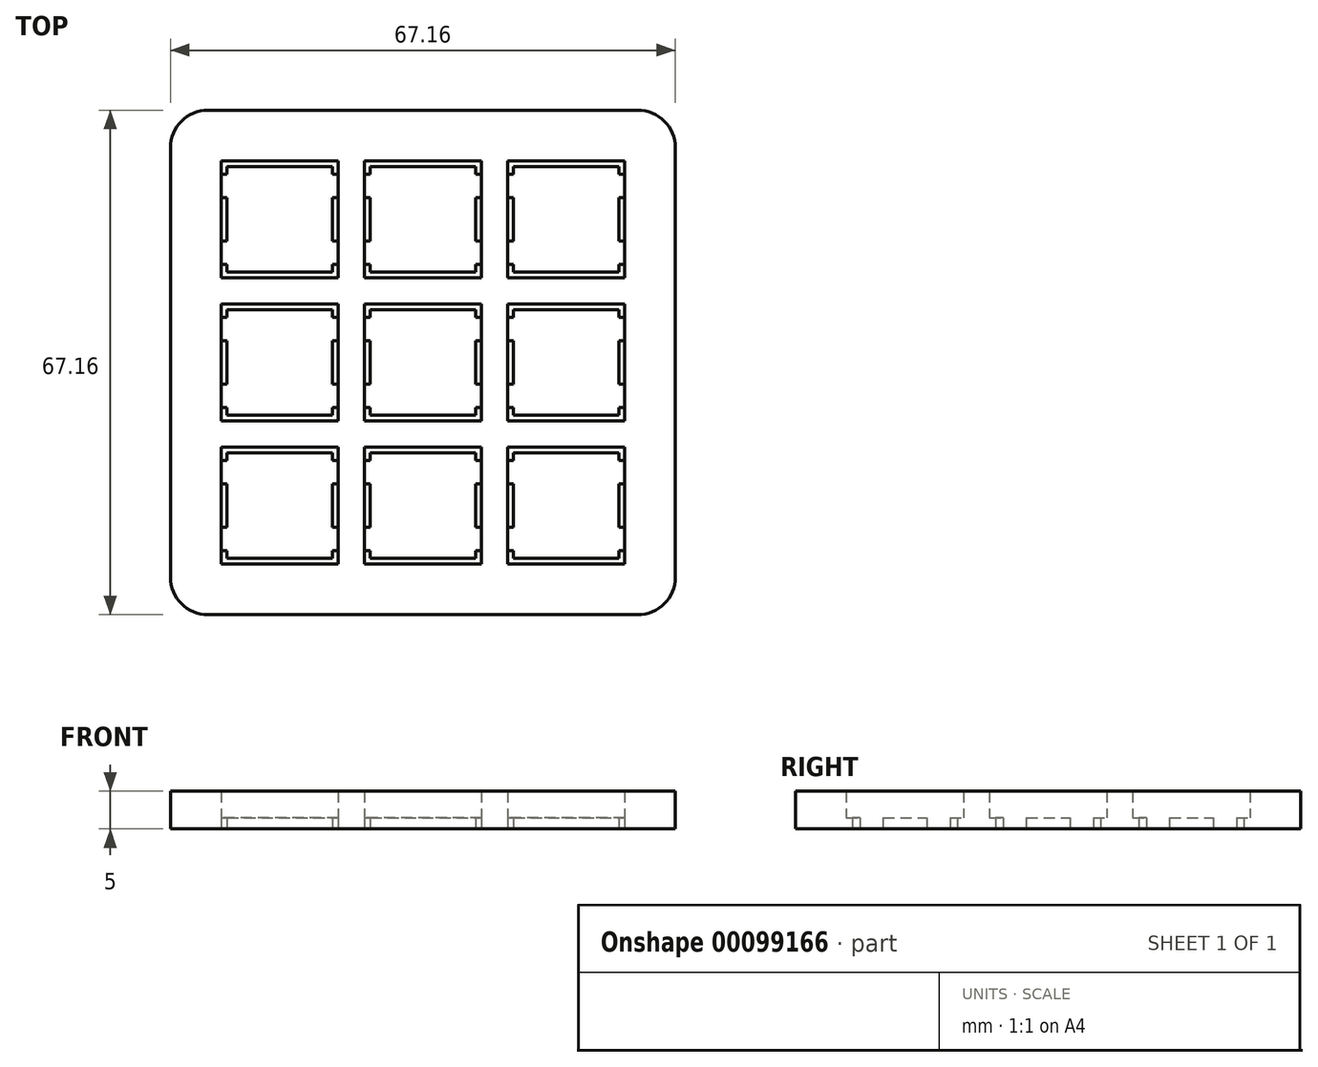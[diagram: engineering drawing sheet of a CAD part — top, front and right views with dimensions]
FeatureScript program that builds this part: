
annotation { "Feature Type Name" : "Feature", "Feature Type Description" : "" }
export const myFeature = defineFeature(function(context is Context, id is Id, definition is map)
    precondition{}
    {
        {
            var Q0;
            Q0=qCreatedBy(makeId("Top.planeOp"),FACE);
            var sketch = newSketch(context, id + "F0", { "sketchPlane" : qUnion([Q0])});
            skLineSegment(sketch, "E0", {"start": v(-33.58, 33.58) * mm, "end": v(33.58, 33.58) * mm});
            skLineSegment(sketch, "E1", {"start": v(33.58, 33.58) * mm, "end": v(33.58, -33.58) * mm});
            skLineSegment(sketch, "E2", {"start": v(33.58, -33.58) * mm, "end": v(-33.58, -33.58) * mm});
            skLineSegment(sketch, "E3", {"start": v(-33.58, -33.58) * mm, "end": v(-33.58, 33.58) * mm});
            skLineSegment(sketch, "E4", {"start": v(-12.05, 13.05) * mm, "end": v(-12.05, 12.05) * mm});
            skLineSegment(sketch, "E5", {"start": v(-12.05, 12.05) * mm, "end": v(-26.05, 12.05) * mm});
            skLineSegment(sketch, "E6", {"start": v(-26.05, 12.05) * mm, "end": v(-26.05, 13.05) * mm});
            skLineSegment(sketch, "E7", {"start": v(-26.05, 13.05) * mm, "end": v(-26.85, 13.05) * mm});
            skLineSegment(sketch, "E8", {"start": v(-26.85, 13.05) * mm, "end": v(-26.85, 16.15) * mm});
            skLineSegment(sketch, "E9", {"start": v(-26.85, 16.15) * mm, "end": v(-26.05, 16.15) * mm});
            skLineSegment(sketch, "E10", {"start": v(-26.05, 16.15) * mm, "end": v(-26.05, 21.95) * mm});
            skLineSegment(sketch, "E11", {"start": v(-26.05, 21.95) * mm, "end": v(-26.85, 21.95) * mm});
            skLineSegment(sketch, "E12", {"start": v(-26.85, 21.95) * mm, "end": v(-26.85, 25.05) * mm});
            skLineSegment(sketch, "E13", {"start": v(-26.85, 25.05) * mm, "end": v(-26.05, 25.05) * mm});
            skLineSegment(sketch, "E14", {"start": v(-26.05, 25.05) * mm, "end": v(-26.05, 26.05) * mm});
            skLineSegment(sketch, "E15", {"start": v(-26.05, 26.05) * mm, "end": v(-12.05, 26.05) * mm});
            skLineSegment(sketch, "E16", {"start": v(-12.05, 26.05) * mm, "end": v(-12.05, 25.05) * mm});
            skLineSegment(sketch, "E17", {"start": v(-12.05, 25.05) * mm, "end": v(-11.25, 25.05) * mm});
            skLineSegment(sketch, "E18", {"start": v(-11.25, 25.05) * mm, "end": v(-11.25, 21.95) * mm});
            skLineSegment(sketch, "E19", {"start": v(-11.25, 21.95) * mm, "end": v(-12.05, 21.95) * mm});
            skLineSegment(sketch, "E20", {"start": v(-12.05, 21.95) * mm, "end": v(-12.05, 16.15) * mm});
            skLineSegment(sketch, "E21", {"start": v(-12.05, 16.15) * mm, "end": v(-11.25, 16.15) * mm});
            skLineSegment(sketch, "E22", {"start": v(-11.25, 16.15) * mm, "end": v(-11.25, 13.05) * mm});
            skLineSegment(sketch, "E23", {"start": v(-11.25, 13.05) * mm, "end": v(-12.05, 13.05) * mm});
            skLineSegment(sketch, "E24", {"start": v(-12.05, -6) * mm, "end": v(-12.05, -7) * mm});
            skLineSegment(sketch, "E25", {"start": v(-12.05, -7) * mm, "end": v(-26.05, -7) * mm});
            skLineSegment(sketch, "E26", {"start": v(-26.05, -7) * mm, "end": v(-26.05, -6) * mm});
            skLineSegment(sketch, "E27", {"start": v(-26.05, -6) * mm, "end": v(-26.85, -6) * mm});
            skLineSegment(sketch, "E28", {"start": v(-26.85, -6) * mm, "end": v(-26.85, -2.9) * mm});
            skLineSegment(sketch, "E29", {"start": v(-26.85, -2.9) * mm, "end": v(-26.05, -2.9) * mm});
            skLineSegment(sketch, "E30", {"start": v(-26.05, -2.9) * mm, "end": v(-26.05, 2.9) * mm});
            skLineSegment(sketch, "E31", {"start": v(-26.05, 2.9) * mm, "end": v(-26.85, 2.9) * mm});
            skLineSegment(sketch, "E32", {"start": v(-26.85, 2.9) * mm, "end": v(-26.85, 6) * mm});
            skLineSegment(sketch, "E33", {"start": v(-26.85, 6) * mm, "end": v(-26.05, 6) * mm});
            skLineSegment(sketch, "E34", {"start": v(-26.05, 6) * mm, "end": v(-26.05, 7) * mm});
            skLineSegment(sketch, "E35", {"start": v(-26.05, 7) * mm, "end": v(-12.05, 7) * mm});
            skLineSegment(sketch, "E36", {"start": v(-12.05, 7) * mm, "end": v(-12.05, 6) * mm});
            skLineSegment(sketch, "E37", {"start": v(-12.05, 6) * mm, "end": v(-11.25, 6) * mm});
            skLineSegment(sketch, "E38", {"start": v(-11.25, 6) * mm, "end": v(-11.25, 2.9) * mm});
            skLineSegment(sketch, "E39", {"start": v(-11.25, 2.9) * mm, "end": v(-12.05, 2.9) * mm});
            skLineSegment(sketch, "E40", {"start": v(-12.05, 2.9) * mm, "end": v(-12.05, -2.9) * mm});
            skLineSegment(sketch, "E41", {"start": v(-12.05, -2.9) * mm, "end": v(-11.25, -2.9) * mm});
            skLineSegment(sketch, "E42", {"start": v(-11.25, -2.9) * mm, "end": v(-11.25, -6) * mm});
            skLineSegment(sketch, "E43", {"start": v(-11.25, -6) * mm, "end": v(-12.05, -6) * mm});
            skLineSegment(sketch, "E44", {"start": v(-12.05, -25.05) * mm, "end": v(-12.05, -26.05) * mm});
            skLineSegment(sketch, "E45", {"start": v(-12.05, -26.05) * mm, "end": v(-26.05, -26.05) * mm});
            skLineSegment(sketch, "E46", {"start": v(-26.05, -26.05) * mm, "end": v(-26.05, -25.05) * mm});
            skLineSegment(sketch, "E47", {"start": v(-26.05, -25.05) * mm, "end": v(-26.85, -25.05) * mm});
            skLineSegment(sketch, "E48", {"start": v(-26.85, -25.05) * mm, "end": v(-26.85, -21.95) * mm});
            skLineSegment(sketch, "E49", {"start": v(-26.85, -21.95) * mm, "end": v(-26.05, -21.95) * mm});
            skLineSegment(sketch, "E50", {"start": v(-26.05, -21.95) * mm, "end": v(-26.05, -16.15) * mm});
            skLineSegment(sketch, "E51", {"start": v(-26.05, -16.15) * mm, "end": v(-26.85, -16.15) * mm});
            skLineSegment(sketch, "E52", {"start": v(-26.85, -16.15) * mm, "end": v(-26.85, -13.05) * mm});
            skLineSegment(sketch, "E53", {"start": v(-26.85, -13.05) * mm, "end": v(-26.05, -13.05) * mm});
            skLineSegment(sketch, "E54", {"start": v(-26.05, -13.05) * mm, "end": v(-26.05, -12.05) * mm});
            skLineSegment(sketch, "E55", {"start": v(-26.05, -12.05) * mm, "end": v(-12.05, -12.05) * mm});
            skLineSegment(sketch, "E56", {"start": v(-12.05, -12.05) * mm, "end": v(-12.05, -13.05) * mm});
            skLineSegment(sketch, "E57", {"start": v(-12.05, -13.05) * mm, "end": v(-11.25, -13.05) * mm});
            skLineSegment(sketch, "E58", {"start": v(-11.25, -13.05) * mm, "end": v(-11.25, -16.15) * mm});
            skLineSegment(sketch, "E59", {"start": v(-11.25, -16.15) * mm, "end": v(-12.05, -16.15) * mm});
            skLineSegment(sketch, "E60", {"start": v(-12.05, -16.15) * mm, "end": v(-12.05, -21.95) * mm});
            skLineSegment(sketch, "E61", {"start": v(-12.05, -21.95) * mm, "end": v(-11.25, -21.95) * mm});
            skLineSegment(sketch, "E62", {"start": v(-11.25, -21.95) * mm, "end": v(-11.25, -25.05) * mm});
            skLineSegment(sketch, "E63", {"start": v(-11.25, -25.05) * mm, "end": v(-12.05, -25.05) * mm});
            skLineSegment(sketch, "E64", {"start": v(7, 13.05) * mm, "end": v(7, 12.05) * mm});
            skLineSegment(sketch, "E65", {"start": v(7, 12.05) * mm, "end": v(-7, 12.05) * mm});
            skLineSegment(sketch, "E66", {"start": v(-7, 12.05) * mm, "end": v(-7, 13.05) * mm});
            skLineSegment(sketch, "E67", {"start": v(-7, 13.05) * mm, "end": v(-7.8, 13.05) * mm});
            skLineSegment(sketch, "E68", {"start": v(-7.8, 13.05) * mm, "end": v(-7.8, 16.15) * mm});
            skLineSegment(sketch, "E69", {"start": v(-7.8, 16.15) * mm, "end": v(-7, 16.15) * mm});
            skLineSegment(sketch, "E70", {"start": v(-7, 16.15) * mm, "end": v(-7, 21.95) * mm});
            skLineSegment(sketch, "E71", {"start": v(-7, 21.95) * mm, "end": v(-7.8, 21.95) * mm});
            skLineSegment(sketch, "E72", {"start": v(-7.8, 21.95) * mm, "end": v(-7.8, 25.05) * mm});
            skLineSegment(sketch, "E73", {"start": v(-7.8, 25.05) * mm, "end": v(-7, 25.05) * mm});
            skLineSegment(sketch, "E74", {"start": v(-7, 25.05) * mm, "end": v(-7, 26.05) * mm});
            skLineSegment(sketch, "E75", {"start": v(-7, 26.05) * mm, "end": v(7, 26.05) * mm});
            skLineSegment(sketch, "E76", {"start": v(7, 26.05) * mm, "end": v(7, 25.05) * mm});
            skLineSegment(sketch, "E77", {"start": v(7, 25.05) * mm, "end": v(7.8, 25.05) * mm});
            skLineSegment(sketch, "E78", {"start": v(7.8, 25.05) * mm, "end": v(7.8, 21.95) * mm});
            skLineSegment(sketch, "E79", {"start": v(7.8, 21.95) * mm, "end": v(7, 21.95) * mm});
            skLineSegment(sketch, "E80", {"start": v(7, 21.95) * mm, "end": v(7, 16.15) * mm});
            skLineSegment(sketch, "E81", {"start": v(7, 16.15) * mm, "end": v(7.8, 16.15) * mm});
            skLineSegment(sketch, "E82", {"start": v(7.8, 16.15) * mm, "end": v(7.8, 13.05) * mm});
            skLineSegment(sketch, "E83", {"start": v(7.8, 13.05) * mm, "end": v(7, 13.05) * mm});
            skLineSegment(sketch, "E84", {"start": v(7, -6) * mm, "end": v(7, -7) * mm});
            skLineSegment(sketch, "E85", {"start": v(7, -7) * mm, "end": v(-7, -7) * mm});
            skLineSegment(sketch, "E86", {"start": v(-7, -7) * mm, "end": v(-7, -6) * mm});
            skLineSegment(sketch, "E87", {"start": v(-7, -6) * mm, "end": v(-7.8, -6) * mm});
            skLineSegment(sketch, "E88", {"start": v(-7.8, -6) * mm, "end": v(-7.8, -2.9) * mm});
            skLineSegment(sketch, "E89", {"start": v(-7.8, -2.9) * mm, "end": v(-7, -2.9) * mm});
            skLineSegment(sketch, "E90", {"start": v(-7, -2.9) * mm, "end": v(-7, 2.9) * mm});
            skLineSegment(sketch, "E91", {"start": v(-7, 2.9) * mm, "end": v(-7.8, 2.9) * mm});
            skLineSegment(sketch, "E92", {"start": v(-7.8, 2.9) * mm, "end": v(-7.8, 6) * mm});
            skLineSegment(sketch, "E93", {"start": v(-7.8, 6) * mm, "end": v(-7, 6) * mm});
            skLineSegment(sketch, "E94", {"start": v(-7, 6) * mm, "end": v(-7, 7) * mm});
            skLineSegment(sketch, "E95", {"start": v(-7, 7) * mm, "end": v(7, 7) * mm});
            skLineSegment(sketch, "E96", {"start": v(7, 7) * mm, "end": v(7, 6) * mm});
            skLineSegment(sketch, "E97", {"start": v(7, 6) * mm, "end": v(7.8, 6) * mm});
            skLineSegment(sketch, "E98", {"start": v(7.8, 6) * mm, "end": v(7.8, 2.9) * mm});
            skLineSegment(sketch, "E99", {"start": v(7.8, 2.9) * mm, "end": v(7, 2.9) * mm});
            skLineSegment(sketch, "E100", {"start": v(7, 2.9) * mm, "end": v(7, -2.9) * mm});
            skLineSegment(sketch, "E101", {"start": v(7, -2.9) * mm, "end": v(7.8, -2.9) * mm});
            skLineSegment(sketch, "E102", {"start": v(7.8, -2.9) * mm, "end": v(7.8, -6) * mm});
            skLineSegment(sketch, "E103", {"start": v(7.8, -6) * mm, "end": v(7, -6) * mm});
            skLineSegment(sketch, "E104", {"start": v(7, -25.05) * mm, "end": v(7, -26.05) * mm});
            skLineSegment(sketch, "E105", {"start": v(7, -26.05) * mm, "end": v(-7, -26.05) * mm});
            skLineSegment(sketch, "E106", {"start": v(-7, -26.05) * mm, "end": v(-7, -25.05) * mm});
            skLineSegment(sketch, "E107", {"start": v(-7, -25.05) * mm, "end": v(-7.8, -25.05) * mm});
            skLineSegment(sketch, "E108", {"start": v(-7.8, -25.05) * mm, "end": v(-7.8, -21.95) * mm});
            skLineSegment(sketch, "E109", {"start": v(-7.8, -21.95) * mm, "end": v(-7, -21.95) * mm});
            skLineSegment(sketch, "E110", {"start": v(-7, -21.95) * mm, "end": v(-7, -16.15) * mm});
            skLineSegment(sketch, "E111", {"start": v(-7, -16.15) * mm, "end": v(-7.8, -16.15) * mm});
            skLineSegment(sketch, "E112", {"start": v(-7.8, -16.15) * mm, "end": v(-7.8, -13.05) * mm});
            skLineSegment(sketch, "E113", {"start": v(-7.8, -13.05) * mm, "end": v(-7, -13.05) * mm});
            skLineSegment(sketch, "E114", {"start": v(-7, -13.05) * mm, "end": v(-7, -12.05) * mm});
            skLineSegment(sketch, "E115", {"start": v(-7, -12.05) * mm, "end": v(7, -12.05) * mm});
            skLineSegment(sketch, "E116", {"start": v(7, -12.05) * mm, "end": v(7, -13.05) * mm});
            skLineSegment(sketch, "E117", {"start": v(7, -13.05) * mm, "end": v(7.8, -13.05) * mm});
            skLineSegment(sketch, "E118", {"start": v(7.8, -13.05) * mm, "end": v(7.8, -16.15) * mm});
            skLineSegment(sketch, "E119", {"start": v(7.8, -16.15) * mm, "end": v(7, -16.15) * mm});
            skLineSegment(sketch, "E120", {"start": v(7, -16.15) * mm, "end": v(7, -21.95) * mm});
            skLineSegment(sketch, "E121", {"start": v(7, -21.95) * mm, "end": v(7.8, -21.95) * mm});
            skLineSegment(sketch, "E122", {"start": v(7.8, -21.95) * mm, "end": v(7.8, -25.05) * mm});
            skLineSegment(sketch, "E123", {"start": v(7.8, -25.05) * mm, "end": v(7, -25.05) * mm});
            skLineSegment(sketch, "E124", {"start": v(26.05, 13.05) * mm, "end": v(26.05, 12.05) * mm});
            skLineSegment(sketch, "E125", {"start": v(26.05, 12.05) * mm, "end": v(12.05, 12.05) * mm});
            skLineSegment(sketch, "E126", {"start": v(12.05, 12.05) * mm, "end": v(12.05, 13.05) * mm});
            skLineSegment(sketch, "E127", {"start": v(12.05, 13.05) * mm, "end": v(11.25, 13.05) * mm});
            skLineSegment(sketch, "E128", {"start": v(11.25, 13.05) * mm, "end": v(11.25, 16.15) * mm});
            skLineSegment(sketch, "E129", {"start": v(11.25, 16.15) * mm, "end": v(12.05, 16.15) * mm});
            skLineSegment(sketch, "E130", {"start": v(12.05, 16.15) * mm, "end": v(12.05, 21.95) * mm});
            skLineSegment(sketch, "E131", {"start": v(12.05, 21.95) * mm, "end": v(11.25, 21.95) * mm});
            skLineSegment(sketch, "E132", {"start": v(11.25, 21.95) * mm, "end": v(11.25, 25.05) * mm});
            skLineSegment(sketch, "E133", {"start": v(11.25, 25.05) * mm, "end": v(12.05, 25.05) * mm});
            skLineSegment(sketch, "E134", {"start": v(12.05, 25.05) * mm, "end": v(12.05, 26.05) * mm});
            skLineSegment(sketch, "E135", {"start": v(12.05, 26.05) * mm, "end": v(26.05, 26.05) * mm});
            skLineSegment(sketch, "E136", {"start": v(26.05, 26.05) * mm, "end": v(26.05, 25.05) * mm});
            skLineSegment(sketch, "E137", {"start": v(26.05, 25.05) * mm, "end": v(26.85, 25.05) * mm});
            skLineSegment(sketch, "E138", {"start": v(26.85, 25.05) * mm, "end": v(26.85, 21.95) * mm});
            skLineSegment(sketch, "E139", {"start": v(26.85, 21.95) * mm, "end": v(26.05, 21.95) * mm});
            skLineSegment(sketch, "E140", {"start": v(26.05, 21.95) * mm, "end": v(26.05, 16.15) * mm});
            skLineSegment(sketch, "E141", {"start": v(26.05, 16.15) * mm, "end": v(26.85, 16.15) * mm});
            skLineSegment(sketch, "E142", {"start": v(26.85, 16.15) * mm, "end": v(26.85, 13.05) * mm});
            skLineSegment(sketch, "E143", {"start": v(26.85, 13.05) * mm, "end": v(26.05, 13.05) * mm});
            skLineSegment(sketch, "E144", {"start": v(26.05, -6) * mm, "end": v(26.05, -7) * mm});
            skLineSegment(sketch, "E145", {"start": v(26.05, -7) * mm, "end": v(12.05, -7) * mm});
            skLineSegment(sketch, "E146", {"start": v(12.05, -7) * mm, "end": v(12.05, -6) * mm});
            skLineSegment(sketch, "E147", {"start": v(12.05, -6) * mm, "end": v(11.25, -6) * mm});
            skLineSegment(sketch, "E148", {"start": v(11.25, -6) * mm, "end": v(11.25, -2.9) * mm});
            skLineSegment(sketch, "E149", {"start": v(11.25, -2.9) * mm, "end": v(12.05, -2.9) * mm});
            skLineSegment(sketch, "E150", {"start": v(12.05, -2.9) * mm, "end": v(12.05, 2.9) * mm});
            skLineSegment(sketch, "E151", {"start": v(12.05, 2.9) * mm, "end": v(11.25, 2.9) * mm});
            skLineSegment(sketch, "E152", {"start": v(11.25, 2.9) * mm, "end": v(11.25, 6) * mm});
            skLineSegment(sketch, "E153", {"start": v(11.25, 6) * mm, "end": v(12.05, 6) * mm});
            skLineSegment(sketch, "E154", {"start": v(12.05, 6) * mm, "end": v(12.05, 7) * mm});
            skLineSegment(sketch, "E155", {"start": v(12.05, 7) * mm, "end": v(26.05, 7) * mm});
            skLineSegment(sketch, "E156", {"start": v(26.05, 7) * mm, "end": v(26.05, 6) * mm});
            skLineSegment(sketch, "E157", {"start": v(26.05, 6) * mm, "end": v(26.85, 6) * mm});
            skLineSegment(sketch, "E158", {"start": v(26.85, 6) * mm, "end": v(26.85, 2.9) * mm});
            skLineSegment(sketch, "E159", {"start": v(26.85, 2.9) * mm, "end": v(26.05, 2.9) * mm});
            skLineSegment(sketch, "E160", {"start": v(26.05, 2.9) * mm, "end": v(26.05, -2.9) * mm});
            skLineSegment(sketch, "E161", {"start": v(26.05, -2.9) * mm, "end": v(26.85, -2.9) * mm});
            skLineSegment(sketch, "E162", {"start": v(26.85, -2.9) * mm, "end": v(26.85, -6) * mm});
            skLineSegment(sketch, "E163", {"start": v(26.85, -6) * mm, "end": v(26.05, -6) * mm});
            skLineSegment(sketch, "E164", {"start": v(26.05, -25.05) * mm, "end": v(26.05, -26.05) * mm});
            skLineSegment(sketch, "E165", {"start": v(26.05, -26.05) * mm, "end": v(12.05, -26.05) * mm});
            skLineSegment(sketch, "E166", {"start": v(12.05, -26.05) * mm, "end": v(12.05, -25.05) * mm});
            skLineSegment(sketch, "E167", {"start": v(12.05, -25.05) * mm, "end": v(11.25, -25.05) * mm});
            skLineSegment(sketch, "E168", {"start": v(11.25, -25.05) * mm, "end": v(11.25, -21.95) * mm});
            skLineSegment(sketch, "E169", {"start": v(11.25, -21.95) * mm, "end": v(12.05, -21.95) * mm});
            skLineSegment(sketch, "E170", {"start": v(12.05, -21.95) * mm, "end": v(12.05, -16.15) * mm});
            skLineSegment(sketch, "E171", {"start": v(12.05, -16.15) * mm, "end": v(11.25, -16.15) * mm});
            skLineSegment(sketch, "E172", {"start": v(11.25, -16.15) * mm, "end": v(11.25, -13.05) * mm});
            skLineSegment(sketch, "E173", {"start": v(11.25, -13.05) * mm, "end": v(12.05, -13.05) * mm});
            skLineSegment(sketch, "E174", {"start": v(12.05, -13.05) * mm, "end": v(12.05, -12.05) * mm});
            skLineSegment(sketch, "E175", {"start": v(12.05, -12.05) * mm, "end": v(26.05, -12.05) * mm});
            skLineSegment(sketch, "E176", {"start": v(26.05, -12.05) * mm, "end": v(26.05, -13.05) * mm});
            skLineSegment(sketch, "E177", {"start": v(26.05, -13.05) * mm, "end": v(26.85, -13.05) * mm});
            skLineSegment(sketch, "E178", {"start": v(26.85, -13.05) * mm, "end": v(26.85, -16.15) * mm});
            skLineSegment(sketch, "E179", {"start": v(26.85, -16.15) * mm, "end": v(26.05, -16.15) * mm});
            skLineSegment(sketch, "E180", {"start": v(26.05, -16.15) * mm, "end": v(26.05, -21.95) * mm});
            skLineSegment(sketch, "E181", {"start": v(26.05, -21.95) * mm, "end": v(26.85, -21.95) * mm});
            skLineSegment(sketch, "E182", {"start": v(26.85, -21.95) * mm, "end": v(26.85, -25.05) * mm});
            skLineSegment(sketch, "E183", {"start": v(26.85, -25.05) * mm, "end": v(26.05, -25.05) * mm});
            skLineSegment(sketch, "E184", {"start": v(-40.38, 26.85) * mm, "end": v(39.04, 26.85) * mm, "construction": true});
            skLineSegment(sketch, "E185.MirrorCS", {"start": v(-40.38, -26.85) * mm, "end": v(39.04, -26.85) * mm, "construction": true});
            skLineSegment(sketch, "E186", {"start": v(39.04, 11.25) * mm, "end": v(-40.38, 11.25) * mm, "construction": true});
            skLineSegment(sketch, "E187.MirrorCS", {"start": v(39.04, -11.25) * mm, "end": v(-40.38, -11.25) * mm, "construction": true});
            skLineSegment(sketch, "E188", {"start": v(39.04, 11.25) * mm, "end": v(39.04, 7.8) * mm, "construction": true});
            skLineSegment(sketch, "E189", {"start": v(39.04, 7.8) * mm, "end": v(-40.38, 7.8) * mm, "construction": true});
            skLineSegment(sketch, "E190.MirrorCS", {"start": v(39.04, -7.8) * mm, "end": v(-40.38, -7.8) * mm, "construction": true});
            skLineSegment(sketch, "E191.bottom", {"start": v(-26.85, 26.85) * mm, "end": v(-11.25, 26.85) * mm});
            skLineSegment(sketch, "E191.top", {"start": v(-26.85, 11.25) * mm, "end": v(-11.25, 11.25) * mm});
            skLineSegment(sketch, "E191.left", {"start": v(-26.85, 26.85) * mm, "end": v(-26.85, 11.25) * mm});
            skLineSegment(sketch, "E191.right", {"start": v(-11.25, 26.85) * mm, "end": v(-11.25, 11.25) * mm});
            skLineSegment(sketch, "E192.bottom", {"start": v(-7.8, 26.85) * mm, "end": v(7.8, 26.85) * mm});
            skLineSegment(sketch, "E192.top", {"start": v(-7.8, 11.25) * mm, "end": v(7.8, 11.25) * mm});
            skLineSegment(sketch, "E192.left", {"start": v(-7.8, 26.85) * mm, "end": v(-7.8, 11.25) * mm});
            skLineSegment(sketch, "E192.right", {"start": v(7.8, 26.85) * mm, "end": v(7.8, 11.25) * mm});
            skLineSegment(sketch, "E193.bottom", {"start": v(11.25, 26.85) * mm, "end": v(26.85, 26.85) * mm});
            skLineSegment(sketch, "E193.top", {"start": v(11.25, 11.25) * mm, "end": v(26.85, 11.25) * mm});
            skLineSegment(sketch, "E193.left", {"start": v(11.25, 26.85) * mm, "end": v(11.25, 11.25) * mm});
            skLineSegment(sketch, "E193.right", {"start": v(26.85, 26.85) * mm, "end": v(26.85, 11.25) * mm});
            skLineSegment(sketch, "E194.bottom", {"start": v(-26.85, 7.8) * mm, "end": v(-11.25, 7.8) * mm});
            skLineSegment(sketch, "E194.top", {"start": v(-26.85, -7.8) * mm, "end": v(-11.25, -7.8) * mm});
            skLineSegment(sketch, "E194.left", {"start": v(-26.85, 7.8) * mm, "end": v(-26.85, -7.8) * mm});
            skLineSegment(sketch, "E194.right", {"start": v(-11.25, 7.8) * mm, "end": v(-11.25, -7.8) * mm});
            skLineSegment(sketch, "E195.bottom", {"start": v(-7.8, 7.8) * mm, "end": v(7.8, 7.8) * mm});
            skLineSegment(sketch, "E195.top", {"start": v(-7.8, -7.8) * mm, "end": v(7.8, -7.8) * mm});
            skLineSegment(sketch, "E195.left", {"start": v(-7.8, 7.8) * mm, "end": v(-7.8, -7.8) * mm});
            skLineSegment(sketch, "E195.right", {"start": v(7.8, 7.8) * mm, "end": v(7.8, -7.8) * mm});
            skLineSegment(sketch, "E196.bottom", {"start": v(11.25, 7.8) * mm, "end": v(26.85, 7.8) * mm});
            skLineSegment(sketch, "E196.top", {"start": v(11.25, -7.8) * mm, "end": v(26.85, -7.8) * mm});
            skLineSegment(sketch, "E196.left", {"start": v(11.25, 7.8) * mm, "end": v(11.25, -7.8) * mm});
            skLineSegment(sketch, "E196.right", {"start": v(26.85, 7.8) * mm, "end": v(26.85, -7.8) * mm});
            skLineSegment(sketch, "E197.bottom", {"start": v(-26.85, -11.25) * mm, "end": v(-11.25, -11.25) * mm});
            skLineSegment(sketch, "E197.top", {"start": v(-26.85, -26.85) * mm, "end": v(-11.25, -26.85) * mm});
            skLineSegment(sketch, "E197.left", {"start": v(-26.85, -11.25) * mm, "end": v(-26.85, -26.85) * mm});
            skLineSegment(sketch, "E197.right", {"start": v(-11.25, -11.25) * mm, "end": v(-11.25, -26.85) * mm});
            skLineSegment(sketch, "E198.bottom", {"start": v(-7.8, -11.25) * mm, "end": v(7.8, -11.25) * mm});
            skLineSegment(sketch, "E198.top", {"start": v(-7.8, -26.85) * mm, "end": v(7.8, -26.85) * mm});
            skLineSegment(sketch, "E198.left", {"start": v(-7.8, -11.25) * mm, "end": v(-7.8, -26.85) * mm});
            skLineSegment(sketch, "E198.right", {"start": v(7.8, -11.25) * mm, "end": v(7.8, -26.85) * mm});
            skLineSegment(sketch, "E199.bottom", {"start": v(11.25, -11.25) * mm, "end": v(26.85, -11.25) * mm});
            skLineSegment(sketch, "E199.top", {"start": v(11.25, -26.85) * mm, "end": v(26.85, -26.85) * mm});
            skLineSegment(sketch, "E199.left", {"start": v(11.25, -11.25) * mm, "end": v(11.25, -26.85) * mm});
            skLineSegment(sketch, "E199.right", {"start": v(26.85, -11.25) * mm, "end": v(26.85, -26.85) * mm});
            skSolve(sketch);
        }
        {
            var Q0;
            Q0=makeQuery(id+"F0.imprint","IMPRINT",FACE,{"disambiguationData":[TD([[makeQuery(id+"F0.imprint","IMPRINT",EDGE,{"derivedFrom":sQuery(id+"F0.wireOp",EDGE,"E0")}),-1.0]])]});
            var Q1;
            {var subQ0=sQuery(id+"F0.wireOp",EDGE,"E9");Q1=makeQuery(id+"F0.imprint","IMPRINT",FACE,{"disambiguationData":[TD([[makeQuery(id+"F0.imprint","IMPRINT",EDGE,{"derivedFrom":subQ0}),1.0]])]});}
            var Q2;
            {var subQ4=sQuery(id+"F0.wireOp",EDGE,"E13");Q2=makeQuery(id+"F0.imprint","IMPRINT",FACE,{"disambiguationData":[TD([[makeQuery(id+"F0.imprint","IMPRINT",EDGE,{"derivedFrom":subQ4}),1.0]])]});}
            var Q3;
            {var subQ0=sQuery(id+"F0.wireOp",EDGE,"E19");Q3=makeQuery(id+"F0.imprint","IMPRINT",FACE,{"disambiguationData":[TD([[makeQuery(id+"F0.imprint","IMPRINT",EDGE,{"derivedFrom":subQ0}),1.0]])]});}
            var Q4;
            Q4=makeQuery(id+"F0.imprint","IMPRINT",FACE,{"disambiguationData":[TD([[makeQuery(id+"F0.imprint","IMPRINT",EDGE,{"derivedFrom":sQuery(id+"F0.wireOp",EDGE,"E4")}),1.0]])]});
            var Q5;
            Q5=makeQuery(id+"F0.imprint","IMPRINT",FACE,{"disambiguationData":[TD([[makeQuery(id+"F0.imprint","IMPRINT",EDGE,{"derivedFrom":sQuery(id+"F0.wireOp",EDGE,"E64")}),1.0]])]});
            var Q6;
            {var subQ0=sQuery(id+"F0.wireOp",EDGE,"E69");Q6=makeQuery(id+"F0.imprint","IMPRINT",FACE,{"disambiguationData":[TD([[makeQuery(id+"F0.imprint","IMPRINT",EDGE,{"derivedFrom":subQ0}),1.0]])]});}
            var Q7;
            {var subQ0=sQuery(id+"F0.wireOp",EDGE,"E73");Q7=makeQuery(id+"F0.imprint","IMPRINT",FACE,{"disambiguationData":[TD([[makeQuery(id+"F0.imprint","IMPRINT",EDGE,{"derivedFrom":subQ0}),1.0]])]});}
            var Q8;
            {var subQ0=sQuery(id+"F0.wireOp",EDGE,"E79");Q8=makeQuery(id+"F0.imprint","IMPRINT",FACE,{"disambiguationData":[TD([[makeQuery(id+"F0.imprint","IMPRINT",EDGE,{"derivedFrom":subQ0}),1.0]])]});}
            var Q9;
            {var subQ0=sQuery(id+"F0.wireOp",EDGE,"E129");Q9=makeQuery(id+"F0.imprint","IMPRINT",FACE,{"disambiguationData":[TD([[makeQuery(id+"F0.imprint","IMPRINT",EDGE,{"derivedFrom":subQ0}),1.0]])]});}
            var Q10;
            {var subQ3=sQuery(id+"F0.wireOp",EDGE,"E133");Q10=makeQuery(id+"F0.imprint","IMPRINT",FACE,{"disambiguationData":[TD([[makeQuery(id+"F0.imprint","IMPRINT",EDGE,{"derivedFrom":subQ3}),1.0]])]});}
            var Q11;
            {var subQ0=sQuery(id+"F0.wireOp",EDGE,"E139");Q11=makeQuery(id+"F0.imprint","IMPRINT",FACE,{"disambiguationData":[TD([[makeQuery(id+"F0.imprint","IMPRINT",EDGE,{"derivedFrom":subQ0}),1.0]])]});}
            var Q12;
            Q12=makeQuery(id+"F0.imprint","IMPRINT",FACE,{"disambiguationData":[TD([[makeQuery(id+"F0.imprint","IMPRINT",EDGE,{"derivedFrom":sQuery(id+"F0.wireOp",EDGE,"E124")}),1.0]])]});
            var Q13;
            {var subQ0=sQuery(id+"F0.wireOp",EDGE,"E153");Q13=makeQuery(id+"F0.imprint","IMPRINT",FACE,{"disambiguationData":[TD([[makeQuery(id+"F0.imprint","IMPRINT",EDGE,{"derivedFrom":subQ0}),1.0]])]});}
            var Q14;
            {var subQ0=sQuery(id+"F0.wireOp",EDGE,"E149");Q14=makeQuery(id+"F0.imprint","IMPRINT",FACE,{"disambiguationData":[TD([[makeQuery(id+"F0.imprint","IMPRINT",EDGE,{"derivedFrom":subQ0}),1.0]])]});}
            var Q15;
            {var subQ0=sQuery(id+"F0.wireOp",EDGE,"E159");Q15=makeQuery(id+"F0.imprint","IMPRINT",FACE,{"disambiguationData":[TD([[makeQuery(id+"F0.imprint","IMPRINT",EDGE,{"derivedFrom":subQ0}),1.0]])]});}
            var Q16;
            Q16=makeQuery(id+"F0.imprint","IMPRINT",FACE,{"disambiguationData":[TD([[makeQuery(id+"F0.imprint","IMPRINT",EDGE,{"derivedFrom":sQuery(id+"F0.wireOp",EDGE,"E144")}),1.0]])]});
            var Q17;
            Q17=makeQuery(id+"F0.imprint","IMPRINT",FACE,{"disambiguationData":[TD([[makeQuery(id+"F0.imprint","IMPRINT",EDGE,{"derivedFrom":sQuery(id+"F0.wireOp",EDGE,"E84")}),1.0]])]});
            var Q18;
            {var subQ0=sQuery(id+"F0.wireOp",EDGE,"E99");Q18=makeQuery(id+"F0.imprint","IMPRINT",FACE,{"disambiguationData":[TD([[makeQuery(id+"F0.imprint","IMPRINT",EDGE,{"derivedFrom":subQ0}),1.0]])]});}
            var Q19;
            {var subQ0=sQuery(id+"F0.wireOp",EDGE,"E93");Q19=makeQuery(id+"F0.imprint","IMPRINT",FACE,{"disambiguationData":[TD([[makeQuery(id+"F0.imprint","IMPRINT",EDGE,{"derivedFrom":subQ0}),1.0]])]});}
            var Q20;
            {var subQ0=sQuery(id+"F0.wireOp",EDGE,"E89");Q20=makeQuery(id+"F0.imprint","IMPRINT",FACE,{"disambiguationData":[TD([[makeQuery(id+"F0.imprint","IMPRINT",EDGE,{"derivedFrom":subQ0}),1.0]])]});}
            var Q21;
            {var subQ0=sQuery(id+"F0.wireOp",EDGE,"E39");Q21=makeQuery(id+"F0.imprint","IMPRINT",FACE,{"disambiguationData":[TD([[makeQuery(id+"F0.imprint","IMPRINT",EDGE,{"derivedFrom":subQ0}),1.0]])]});}
            var Q22;
            {var subQ3=sQuery(id+"F0.wireOp",EDGE,"E33");Q22=makeQuery(id+"F0.imprint","IMPRINT",FACE,{"disambiguationData":[TD([[makeQuery(id+"F0.imprint","IMPRINT",EDGE,{"derivedFrom":subQ3}),1.0]])]});}
            var Q23;
            {var subQ0=sQuery(id+"F0.wireOp",EDGE,"E29");Q23=makeQuery(id+"F0.imprint","IMPRINT",FACE,{"disambiguationData":[TD([[makeQuery(id+"F0.imprint","IMPRINT",EDGE,{"derivedFrom":subQ0}),1.0]])]});}
            var Q24;
            Q24=makeQuery(id+"F0.imprint","IMPRINT",FACE,{"disambiguationData":[TD([[makeQuery(id+"F0.imprint","IMPRINT",EDGE,{"derivedFrom":sQuery(id+"F0.wireOp",EDGE,"E24")}),1.0]])]});
            var Q25;
            {var subQ1=sQuery(id+"F0.wireOp",EDGE,"E53");Q25=makeQuery(id+"F0.imprint","IMPRINT",FACE,{"disambiguationData":[TD([[makeQuery(id+"F0.imprint","IMPRINT",EDGE,{"derivedFrom":subQ1}),1.0]])]});}
            var Q26;
            {var subQ0=sQuery(id+"F0.wireOp",EDGE,"E49");Q26=makeQuery(id+"F0.imprint","IMPRINT",FACE,{"disambiguationData":[TD([[makeQuery(id+"F0.imprint","IMPRINT",EDGE,{"derivedFrom":subQ0}),1.0]])]});}
            var Q27;
            Q27=makeQuery(id+"F0.imprint","IMPRINT",FACE,{"disambiguationData":[TD([[makeQuery(id+"F0.imprint","IMPRINT",EDGE,{"derivedFrom":sQuery(id+"F0.wireOp",EDGE,"E44")}),1.0]])]});
            var Q28;
            {var subQ0=sQuery(id+"F0.wireOp",EDGE,"E59");Q28=makeQuery(id+"F0.imprint","IMPRINT",FACE,{"disambiguationData":[TD([[makeQuery(id+"F0.imprint","IMPRINT",EDGE,{"derivedFrom":subQ0}),1.0]])]});}
            var Q29;
            {var subQ0=sQuery(id+"F0.wireOp",EDGE,"E113");Q29=makeQuery(id+"F0.imprint","IMPRINT",FACE,{"disambiguationData":[TD([[makeQuery(id+"F0.imprint","IMPRINT",EDGE,{"derivedFrom":subQ0}),1.0]])]});}
            var Q30;
            {var subQ0=sQuery(id+"F0.wireOp",EDGE,"E109");Q30=makeQuery(id+"F0.imprint","IMPRINT",FACE,{"disambiguationData":[TD([[makeQuery(id+"F0.imprint","IMPRINT",EDGE,{"derivedFrom":subQ0}),1.0]])]});}
            var Q31;
            Q31=makeQuery(id+"F0.imprint","IMPRINT",FACE,{"disambiguationData":[TD([[makeQuery(id+"F0.imprint","IMPRINT",EDGE,{"derivedFrom":sQuery(id+"F0.wireOp",EDGE,"E104")}),1.0]])]});
            var Q32;
            {var subQ0=sQuery(id+"F0.wireOp",EDGE,"E119");Q32=makeQuery(id+"F0.imprint","IMPRINT",FACE,{"disambiguationData":[TD([[makeQuery(id+"F0.imprint","IMPRINT",EDGE,{"derivedFrom":subQ0}),1.0]])]});}
            var Q33;
            {var subQ0=sQuery(id+"F0.wireOp",EDGE,"E169");Q33=makeQuery(id+"F0.imprint","IMPRINT",FACE,{"disambiguationData":[TD([[makeQuery(id+"F0.imprint","IMPRINT",EDGE,{"derivedFrom":subQ0}),1.0]])]});}
            var Q34;
            {var subQ0=sQuery(id+"F0.wireOp",EDGE,"E173");Q34=makeQuery(id+"F0.imprint","IMPRINT",FACE,{"disambiguationData":[TD([[makeQuery(id+"F0.imprint","IMPRINT",EDGE,{"derivedFrom":subQ0}),1.0]])]});}
            var Q35;
            {var subQ0=sQuery(id+"F0.wireOp",EDGE,"E179");Q35=makeQuery(id+"F0.imprint","IMPRINT",FACE,{"disambiguationData":[TD([[makeQuery(id+"F0.imprint","IMPRINT",EDGE,{"derivedFrom":subQ0}),1.0]])]});}
            var Q36;
            Q36=makeQuery(id+"F0.imprint","IMPRINT",FACE,{"disambiguationData":[TD([[makeQuery(id+"F0.imprint","IMPRINT",EDGE,{"derivedFrom":sQuery(id+"F0.wireOp",EDGE,"E164")}),1.0]])]});
            extrude(context, id + "F1", {"entities" : qUnion([Q0, Q1, Q2, Q3, Q4, Q5, Q6, Q7, Q8, Q9, Q10, Q11, Q12, Q13, Q14, Q15, Q16, Q17, Q18, Q19, Q20, Q21, Q22, Q23, Q24, Q25, Q26, Q27, Q28, Q29, Q30, Q31, Q32, Q33, Q34, Q35, Q36]), "depth" : 1.5 * mm});
        }
        {
            var Q0;
            Q0=makeQuery(id+"F0.imprint","IMPRINT",FACE,{"disambiguationData":[TD([[makeQuery(id+"F0.imprint","IMPRINT",EDGE,{"derivedFrom":sQuery(id+"F0.wireOp",EDGE,"E0")}),-1.0]])]});
            extrude(context, id + "F2", {"entities" : qUnion([Q0]), "operationType" : NewBodyOperationType.ADD, "depth" : 5 * mm});
        }
        {
            var Q0;
            {var subQ0=sQuery(id+"F0.wireOp",EDGE,"E2");var subQ1=sQuery(id+"F0.wireOp",EDGE,"E1");Q0=makeQuery(id+"F2.boolean.opBoolean","MERGE",EDGE,{"derivedFrom":[makeQuery(id+"F1.opExtrude","SWEPT_EDGE",EDGE,{"disambiguationData":[OSD([subQ1,subQ0])]}),makeQuery(id+"F2.opExtrude","SWEPT_EDGE",EDGE,{"disambiguationData":[OSD([subQ1,subQ0])]})]});}
            var Q1;
            {var subQ0=sQuery(id+"F0.wireOp",EDGE,"E1");var subQ1=sQuery(id+"F0.wireOp",EDGE,"E0");Q1=makeQuery(id+"F2.boolean.opBoolean","MERGE",EDGE,{"derivedFrom":[makeQuery(id+"F1.opExtrude","SWEPT_EDGE",EDGE,{"disambiguationData":[OSD([subQ1,subQ0])]}),makeQuery(id+"F2.opExtrude","SWEPT_EDGE",EDGE,{"disambiguationData":[OSD([subQ1,subQ0])]})]});}
            var Q2;
            {var subQ0=sQuery(id+"F0.wireOp",EDGE,"E3");var subQ1=sQuery(id+"F0.wireOp",EDGE,"E2");Q2=makeQuery(id+"F2.boolean.opBoolean","MERGE",EDGE,{"derivedFrom":[makeQuery(id+"F1.opExtrude","SWEPT_EDGE",EDGE,{"disambiguationData":[OSD([subQ1,subQ0])]}),makeQuery(id+"F2.opExtrude","SWEPT_EDGE",EDGE,{"disambiguationData":[OSD([subQ1,subQ0])]})]});}
            var Q3;
            {var subQ0=sQuery(id+"F0.wireOp",EDGE,"E3");var subQ1=sQuery(id+"F0.wireOp",EDGE,"E0");Q3=makeQuery(id+"F2.boolean.opBoolean","MERGE",EDGE,{"derivedFrom":[makeQuery(id+"F1.opExtrude","SWEPT_EDGE",EDGE,{"disambiguationData":[OSD([subQ1,subQ0])]}),makeQuery(id+"F2.opExtrude","SWEPT_EDGE",EDGE,{"disambiguationData":[OSD([subQ1,subQ0])]})]});}
            fillet(context, id + "F3", {"entities" : qUnion([Q0, Q1, Q2, Q3]), "radius" : 5 * mm, "tangentPropagation" : true, "allowEdgeOverflow" : false});
        }
    });
